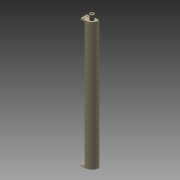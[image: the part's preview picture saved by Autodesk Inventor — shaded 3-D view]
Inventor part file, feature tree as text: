
AUTODESK INVENTOR PART (.ipt)
format: ipt  version: 2015 (Build 190159000, 159)  size: 180,736 bytes
history: native  units: mm
features: extrude x8, sketch x8, pattern_linear x2, shell x1, thread x1, chamfer x1
ambient origin geometry x8: Origin, YZ Plane, XZ Plane, XY Plane, X Axis, Y Axis, Z Axis, Center Point
bodies: 实体1 (feature_tree)
feature tree (21):
  extrude  "拉伸1"  Depth=480.0mm TaperAngle=0.0deg
  shell  "抽壳1"  Thickness=2.0mm
  extrude  "拉伸2"  Depth=5.0mm TaperAngle=0.0deg
  extrude  "拉伸3"  Depth=20.0mm TaperAngle=0.0deg
  extrude  "拉伸4"  Depth=20.0mm TaperAngle=0.0deg
  thread  "螺纹1"  [1 undecoded]
  chamfer  "倒角1"  Distance=2.0mm Angle=45.0deg
  extrude  "拉伸5"  Depth=5.0mm
  extrude  "拉伸6"  Depth=5.0mm
  extrude  "拉伸7"  Depth=7.5mm
  extrude  "拉伸8"  Depth=5.0mm TaperAngle=0.0deg
  pattern_linear  "矩形阵列1"  Spacing1=4.0mm  [1 undecoded]
  pattern_linear  "矩形阵列2"  Spacing1=5.0mm  [1 undecoded]
  sketch  "草图1"  dims[d0=28.0mm d1=480.0mm d2=0.0mm d3=2.0mm]
  sketch  "草图2"  dims[d4=15.0mm d5=5.0mm d6=0.0mm]
  sketch  "草图3"  dims[d7=15.0mm d8=20.0mm d9=0.0mm]
  sketch  "草图4"  dims[d10=10.0mm d11=20.0mm d12=0.0mm d13=10.0mm d14=0.0mm d15=0.5mm d16=2.0mm d17=45.0deg]
  sketch  "草图5"  dims[d18=5.0mm d19=0.0mm d20=5.0mm]
  sketch  "草图6"  dims[d21=5.0mm d22=9.0mm]
  sketch  "草图7"  dims[d23=5.0mm d24=7.5mm]
  sketch  "草图8"  dims[d25=7.5mm d26=5.0mm d27=0.0mm d28=4.0mm d29=5.0mm d30=0.0mm d31=20.0mm d32=2.0mm d33=15.0mm d34=2.0mm d35=0.0mm d36=20.0mm d38=70.0mm d39=40.0mm d41=120.0mm]
note: 3 required parameter values undecoded (feature->parameter linkage not recoverable at this tier; creation-order binding heuristic only, values carry confidence <= 0.55)
